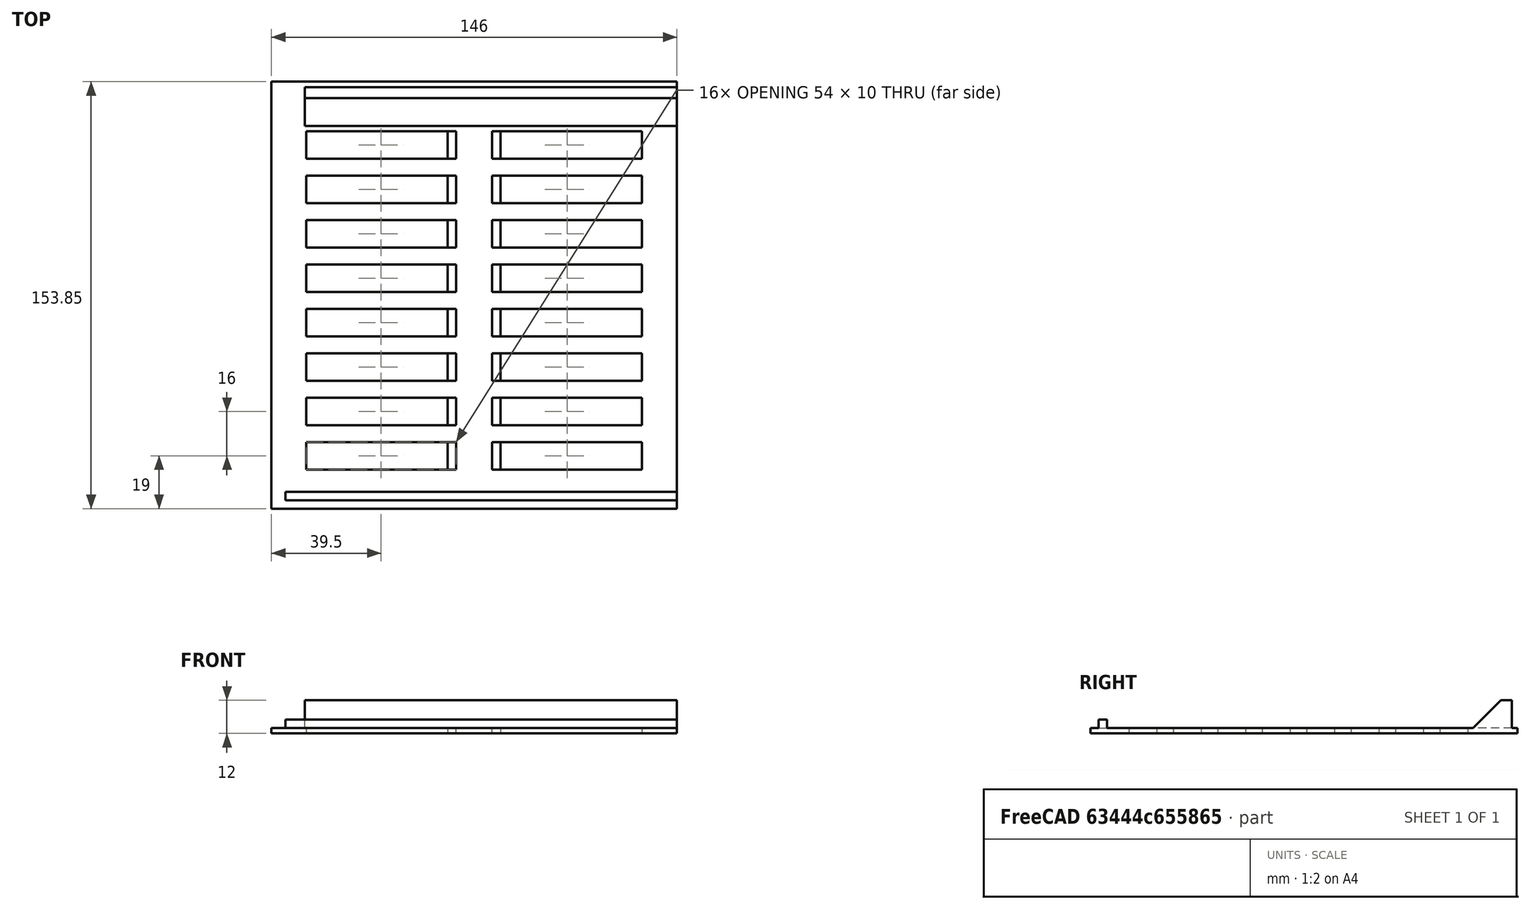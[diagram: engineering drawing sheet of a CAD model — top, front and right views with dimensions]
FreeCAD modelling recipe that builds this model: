
FCSTD DOCUMENT  (FreeCAD 0.17R13522 (Git))
Label: letras_izquierda_v2
License: CreativeCommons Attribution-ShareAlike
LicenseURL: http://creativecommons.org/licenses/by-sa/4.0/
objects: Part::Feature×6, Part::MultiFuse×4, Part::Box×1, Part::FeaturePython×1, Part::Cut×1
note: 13 computed .brp shape members not serialized (recipe doc carries the construction recipe); baked Part::Feature solids carry a one-line shape summary decoded from their .brp

FEATURE [Part::Feature] Cut001
  shape: bbox 30 x 153.9 x 12 mm, 47 faces (baked)
FEATURE [Part::Feature] Cut001001  label="Cut002"
  Placement = pos=(-32,0,0) rot=(0,0,1;0rad)
  shape: bbox 67 x 153.9 x 12 mm, 79 faces (baked)
FEATURE [Part::Feature] Cut001002
  Placement = pos=(-64,0,0) rot=(0,0,1;0rad)
  shape: bbox 47 x 153.9 x 12 mm, 47 faces (baked)
FEATURE [Part::Feature] Cut001003
  Placement = pos=(-34,0,0) rot=(0,0,1;0rad)
  shape: bbox 67 x 153.9 x 12 mm, 79 faces (baked)
FEATURE [Part::Feature] Cut001004
  Placement = pos=(-30,0,0) rot=(0,0,1;0rad)
  shape: bbox 67 x 153.9 x 12 mm, 79 faces (baked)
FEATURE [Part::MultiFuse] Fusion
  Shapes = -> [Cut001,Cut001001]
FEATURE [Part::MultiFuse] Fusion001
  Shapes = -> [Fusion,Cut001004]
FEATURE [Part::MultiFuse] Fusion002
  Shapes = -> [Fusion001,Cut001003]
FEATURE [Part::MultiFuse] Fusion003
  Shapes = -> [Fusion002,Cut001002]
FEATURE [Part::Feature] Fusion003001  label="Fusion004"
  shape: bbox 146 x 153.9 x 12 mm, 79 faces (baked)
FEATURE [Part::Box] Box  label="Cube"
  AttacherType = Attacher::AttachEngine3D
  Height = 10
  Length = 4.5
  Placement = pos=(63,14,-62) rot=(0,0,1;0rad)
  Width = 10
FEATURE [Part::FeaturePython] Array  # Draft array (typed FeaturePython)
  Angle = 360
  ArrayType = 0
  Axis = (0,0,1)
  Base = -> Box
  Center = (0,0,0)
  Fuse = false
  IntervalAxis = (0,0,0)
  IntervalX = (17.5,0,0)
  IntervalY = (0,16,0)
  IntervalZ = (0,0,0)
  NumberPolar = 1
  NumberX = 2
  NumberY = 8
  NumberZ = 1
  Placement = pos=(-1,0,0) rot=(0,0,1;0rad)
FEATURE [Part::Cut] Cut
  Base = -> Fusion003001
  Tool = -> Array
